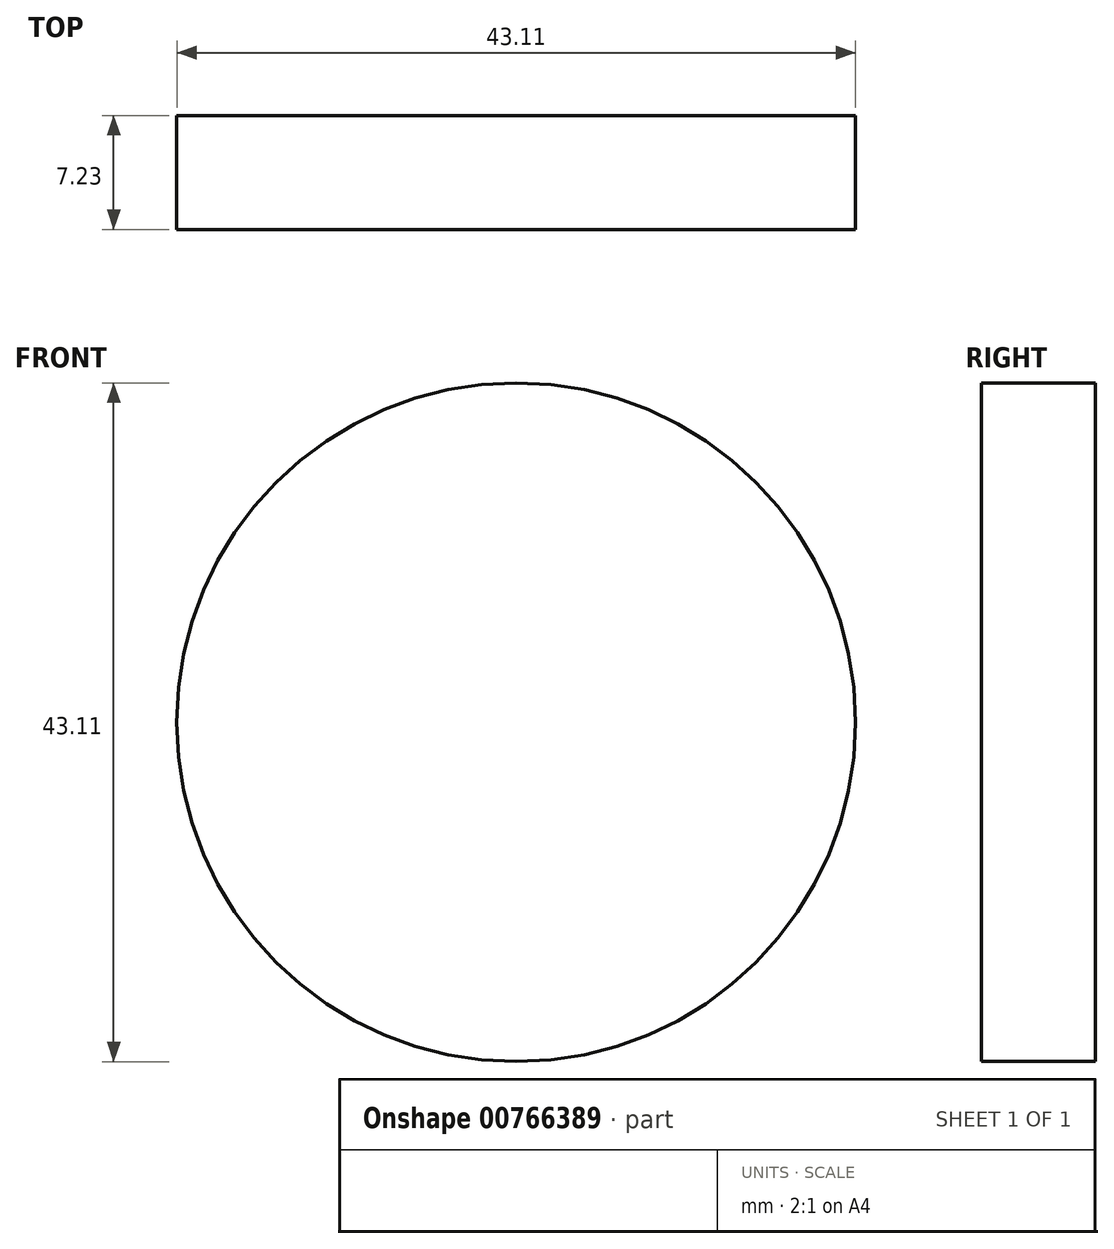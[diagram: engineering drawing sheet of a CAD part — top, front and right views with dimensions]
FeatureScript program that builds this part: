
annotation { "Feature Type Name" : "Feature", "Feature Type Description" : "" }
export const myFeature = defineFeature(function(context is Context, id is Id, definition is map)
    precondition{}
    {
        {
            var Q0;
            Q0=qCreatedBy(makeId("Front.planeOp"),FACE);
            var sketch = newSketch(context, id + "F0", { "sketchPlane" : qUnion([Q0])});
            skCircle(sketch, "E0", {"center": v(-23.96, 18.67) * mm, "radius": 21.56 * mm});
            skSolve(sketch);
        }
        {
            var Q0;
            Q0=makeQuery(id+"F0.imprint","IMPRINT",FACE,{"disambiguationData":[TD([[makeQuery(id+"F0.imprint","IMPRINT",EDGE,{"derivedFrom":sQuery(id+"F0.wireOp",EDGE,"E0")}),1.0]])]});
            extrude(context, id + "F1", {"entities" : qUnion([Q0]), "oppositeDirection" : true, "depth" : 7.23 * mm, "offsetDistance" : 25.4 * mm});
        }
    });
